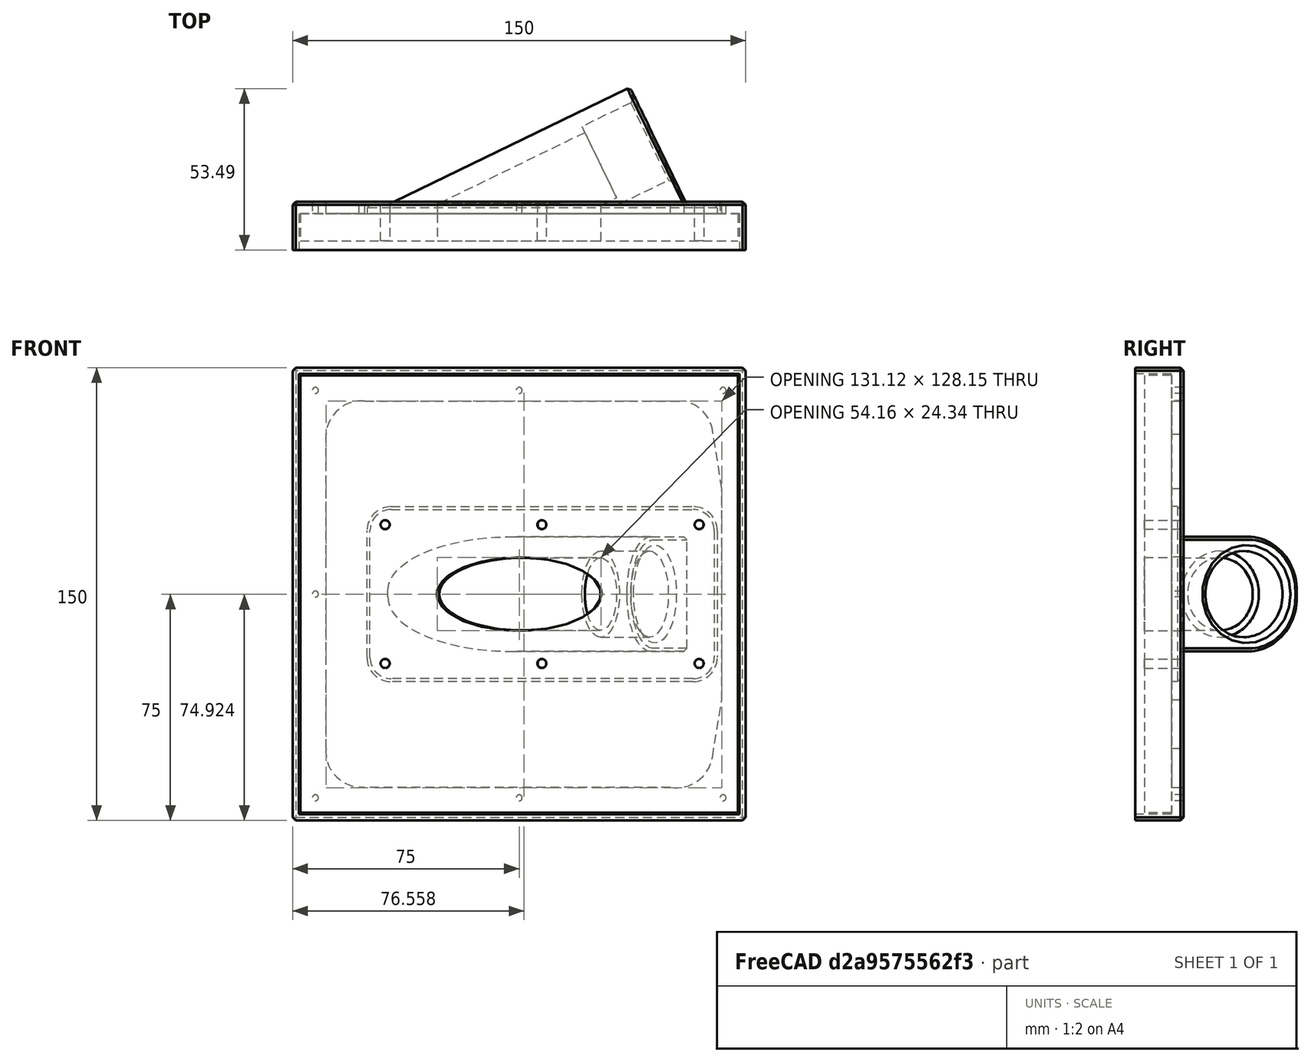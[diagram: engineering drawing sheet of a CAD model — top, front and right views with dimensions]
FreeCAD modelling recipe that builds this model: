
FCSTD DOCUMENT  (FreeCAD 0.19R)
Label: support_panneau_solaire_haut
License: All rights reserved
LicenseURL: http://en.wikipedia.org/wiki/All_rights_reserved
objects: Sketcher::SketchObject×8, PartDesign::Pad×5, PartDesign::Chamfer×4, PartDesign::Pocket×3, PartDesign::Body×3, PartDesign::Fillet×2, Mesh::Feature×2
note: 39 computed .brp shape members not serialized (recipe doc carries the construction recipe); baked Part::Feature solids carry a one-line shape summary decoded from their .brp

FEATURE [Sketcher::SketchObject] Sketch
  FullyConstrained = false
  MapMode = 5
  Support = -> [XY_Plane]
  sketch-geometry (3):
    g0: LineSegment StartX=19 StartY=-50 StartZ=0 EndX=19 EndY=39.129 EndZ=0
    g1: LineSegment StartX=19 StartY=39.129 StartZ=0 EndX=-24.2787 EndY=-50 EndZ=0
    g2: LineSegment StartX=-24.2787 StartY=-50 StartZ=0 EndX=19 EndY=-50 EndZ=0
  constraints (9):
    c: Horizontal(g2)
    c: Coincident(g0,g1)
    c: DistanceX(g-2,g0) = 19
    c: Vertical(g0)
    c: Angle(g1,g0) = 0.45204
    c: Coincident(g1,g2)
    c: Coincident(g2,g0)
    c: PointOnObject(g-1,g1)
    c: Distance(g-1,g2) = 50
FEATURE [PartDesign::Pad] Pad
  AllowMultiFace = false
  Direction = (1,1,1)
  Length = 38
  Length2 = 100
  Midplane = true
  Profile = -> Sketch
  Type = 0
FEATURE [Sketcher::SketchObject] Sketch001
  FullyConstrained = false
  MapMode = 5
  Placement = pos=(0,-50,0) rot=(1,0,0;1.5708rad)
  Support = -> [Pad]
  sketch-geometry (1):
    g0: Circle CenterX=0 CenterY=0 CenterZ=0 NormalX=0 NormalY=0 NormalZ=1 AngleXU=0 Radius=12
  constraints (2):
    c: Coincident(g0,g-1)
    c: Radius(g0) = 12
FEATURE [PartDesign::Pocket] Pocket
  AllowMultiFace = false
  BaseFeature = -> Pad
  Length = 100
  Length2 = 100
  Profile = -> Sketch001
  Type = 0
FEATURE [PartDesign::Fillet] Fillet
  Base = -> Pocket [Edge4,Edge3]
  BaseFeature = -> Pocket
  Radius = 18
  SupportTransform = false
FEATURE [Sketcher::SketchObject] Sketch002
  ExternalGeometry = -> [Fillet]
  FullyConstrained = false
  MapMode = 5
  Placement = pos=(0,-50,0) rot=(1,0,0;1.5708rad)
  Support = -> [Fillet]
  sketch-geometry (1):
    g0: Circle CenterX=0 CenterY=0 CenterZ=0 NormalX=0 NormalY=0 NormalZ=1 AngleXU=0 Radius=14.25
  constraints (2):
    c: Coincident(g0,g-1)
    c: Radius(g0) = 14.25
FEATURE [PartDesign::Pocket] Pocket001
  AllowMultiFace = false
  BaseFeature = -> Fillet
  Length = 20
  Length2 = 100
  Profile = -> Sketch002
  Type = 0
FEATURE [Sketcher::SketchObject] Sketch003
  ExternalGeometry = -> [Pocket001]
  FullyConstrained = true
  MapMode = 5
  Placement = pos=(-3.2e-15,1.6e-15,0) rot=(-0.404812,0.646578,0.646578;3.91089rad)
  Support = -> [Pocket001]
  sketch-geometry (14):
    g0: LineSegment StartX=-50.4171 StartY=29 StartZ=0 EndX=65.5829 EndY=29 EndZ=0
    g1: LineSegment StartX=65.5829 StartY=29 StartZ=0 EndX=65.5829 EndY=-29 EndZ=0
    g2: LineSegment StartX=65.5829 StartY=-29 StartZ=0 EndX=-50.4171 EndY=-29 EndZ=0
    g3: LineSegment StartX=-50.4171 StartY=-29 StartZ=0 EndX=-50.4171 EndY=29 EndZ=0
    g4: Circle CenterX=-44.4171 CenterY=23 CenterZ=0 NormalX=0 NormalY=0 NormalZ=1 AngleXU=0 Radius=1.5
    g5: Circle CenterX=-44.4171 CenterY=-23 CenterZ=0 NormalX=0 NormalY=0 NormalZ=1 AngleXU=0 Radius=1.5
    g6: Circle CenterX=59.5829 CenterY=23 CenterZ=0 NormalX=0 NormalY=0 NormalZ=1 AngleXU=0 Radius=1.5
    g7: Circle CenterX=59.5829 CenterY=-23 CenterZ=0 NormalX=0 NormalY=0 NormalZ=1 AngleXU=0 Radius=1.5
    g8: Circle CenterX=7.58287 CenterY=-23 CenterZ=0 NormalX=0 NormalY=0 NormalZ=1 AngleXU=0 Radius=1.5
    g9: Circle CenterX=7.58287 CenterY=23 CenterZ=0 NormalX=0 NormalY=0 NormalZ=1 AngleXU=0 Radius=1.5
    g10: LineSegment StartX=-44.4171 StartY=23 StartZ=0 EndX=59.5829 EndY=23 EndZ=0
    g11: LineSegment StartX=59.5829 StartY=23 StartZ=0 EndX=59.5829 EndY=-23 EndZ=0
    g12: LineSegment StartX=59.5829 StartY=-23 StartZ=0 EndX=-44.4171 EndY=-23 EndZ=0
    g13: LineSegment StartX=-44.4171 StartY=-23 StartZ=0 EndX=-44.4171 EndY=23 EndZ=0
  constraints (35):
    c: Coincident(g0,g1)
    c: Coincident(g1,g2)
    c: Coincident(g2,g3)
    c: Coincident(g3,g0)
    c: Horizontal(g2)
    c: Vertical(g1)
    c: Symmetric(g0,g2,g-1)
    c: Distance(g0,g-4) = 10
    c: Distance(g-4,g0) = 10
    c: Horizontal(g0)
    c: Coincident(g10,g11)
    c: Coincident(g11,g12)
    c: Coincident(g12,g13)
    c: Coincident(g13,g10)
    c: Horizontal(g10)
    c: Horizontal(g12)
    c: Vertical(g11)
    c: Coincident(g10,g4)
    c: Coincident(g11,g7)
    c: Coincident(g6,g10)
    c: PointOnObject(g9,g10)
    c: Coincident(g5,g12)
    c: Symmetric(g5,g4,g-1)
    c: Symmetric(g9,g8,g-1)
    c: Distance(g4,g0) = 6
    c: Distance(g4,g3) = 6
    c: Distance(g6,g1) = 6
    c: Radius(g4) = 1.5
    c: Equal(g4,g9)
    c: Equal(g4,g6)
    c: Equal(g4,g7)
    c: Equal(g4,g8)
    c: Equal(g4,g5)
    c: DistanceX(g12,g12) = 104
    c: Distance(g4,g9) = 52
FEATURE [PartDesign::Pad] Pad001
  AllowMultiFace = false
  BaseFeature = -> Pocket001
  Direction = (1,1,1)
  Length = 3
  Length2 = 100
  Profile = -> Sketch003
  Type = 0
FEATURE [Sketcher::SketchObject] Sketch009
  FullyConstrained = true
  MapMode = 5
  Placement = pos=(0,0,0) rot=(1,0,0;1.5708rad)
  Support = -> [XZ_Plane001]
  sketch-geometry (8):
    g0: LineSegment StartX=-73 StartY=73 StartZ=0 EndX=73 EndY=73 EndZ=0
    g1: LineSegment StartX=73 StartY=73 StartZ=0 EndX=73 EndY=-73 EndZ=0
    g2: LineSegment StartX=73 StartY=-73 StartZ=0 EndX=-73 EndY=-73 EndZ=0
    g3: LineSegment StartX=-73 StartY=-73 StartZ=0 EndX=-73 EndY=73 EndZ=0
    g4: LineSegment StartX=-75 StartY=75 StartZ=0 EndX=75 EndY=75 EndZ=0
    g5: LineSegment StartX=75 StartY=75 StartZ=0 EndX=75 EndY=-75 EndZ=0
    g6: LineSegment StartX=75 StartY=-75 StartZ=0 EndX=-75 EndY=-75 EndZ=0
    g7: LineSegment StartX=-75 StartY=-75 StartZ=0 EndX=-75 EndY=75 EndZ=0
  constraints (20):
    c: Coincident(g0,g1)
    c: Coincident(g1,g2)
    c: Coincident(g2,g3)
    c: Coincident(g3,g0)
    c: Horizontal(g2)
    c: Vertical(g1)
    c: Symmetric(g0,g2,g-1)
    c: Symmetric(g0,g0,g-2)
    c: Equal(g0,g3)
    c: DistanceY(g3,g3) = 146
    c: Coincident(g4,g5)
    c: Coincident(g5,g6)
    c: Coincident(g6,g7)
    c: Coincident(g7,g4)
    c: Horizontal(g6)
    c: Vertical(g7)
    c: Distance(g4,g3) = 2
    c: Distance(g4,g0) = 2
    c: Symmetric(g4,g4,g-2)
    c: Symmetric(g4,g5,g-1)
FEATURE [PartDesign::Pad] Pad003
  AllowMultiFace = false
  Direction = (1,1,1)
  Length = 12
  Length2 = 100
  Placement = pos=(0,0,0) rot=(1,0,0;1.5708rad)
  Profile = -> Sketch009
  Type = 0
FEATURE [Sketcher::SketchObject] Sketch010
  ExternalGeometry = -> [Pad003]
  FullyConstrained = true
  MapMode = 5
  Placement = pos=(0,0,0) rot=(-1,0,0;1.5708rad)
  Support = -> [Pad003]
  sketch-geometry (21):
    g0: LineSegment StartX=-75 StartY=75 StartZ=0 EndX=75 EndY=75 EndZ=0
    g1: LineSegment StartX=75 StartY=75 StartZ=0 EndX=75 EndY=-75 EndZ=0
    g2: LineSegment StartX=75 StartY=-75 StartZ=0 EndX=-75 EndY=-75 EndZ=0
    g3: LineSegment StartX=-75 StartY=-75 StartZ=0 EndX=-75 EndY=75 EndZ=0
    g4: ArcOfCircle CenterX=-52.0386 CenterY=52.0386 CenterZ=0 NormalX=0 NormalY=0 NormalZ=1 AngleXU=0 Radius=12 StartAngle=1.651 EndAngle=3.2218
    g5: ArcOfCircle CenterX=52.0386 CenterY=52.0386 CenterZ=0 NormalX=0 NormalY=0 NormalZ=1 AngleXU=0 Radius=12.1212 StartAngle=0.162533 EndAngle=1.73333
    g6: ArcOfCircle CenterX=52.0386 CenterY=-52.0386 CenterZ=0 NormalX=0 NormalY=0 NormalZ=1 AngleXU=0 Radius=12.2353 StartAngle=4.92436 EndAngle=6.12218
    g7: ArcOfCircle CenterX=-52.0386 CenterY=-52.0386 CenterZ=0 NormalX=0 NormalY=0 NormalZ=1 AngleXU=0 Radius=12 StartAngle=3.2218 EndAngle=4.79259
    g8: LineSegment StartX=-64 StartY=51.0772 StartZ=0 EndX=-64 EndY=-53 EndZ=0
    g9: LineSegment StartX=-51.0772 StartY=-64 StartZ=0 EndX=54.6127 EndY=-64 EndZ=0
    g10: LineSegment StartX=50.0772 StartY=64 StartZ=0 EndX=-53 EndY=64 EndZ=0
    g11: Circle CenterX=-67.5 CenterY=67.5 CenterZ=0 NormalX=0 NormalY=0 NormalZ=1 AngleXU=0 Radius=1
    g12: Circle CenterX=67.5 CenterY=67.5 CenterZ=0 NormalX=0 NormalY=0 NormalZ=1 AngleXU=0 Radius=1
    g13: Circle CenterX=0 CenterY=67.5 CenterZ=0 NormalX=0 NormalY=0 NormalZ=1 AngleXU=0 Radius=1
    g14: Circle CenterX=-67.5 CenterY=0 CenterZ=0 NormalX=0 NormalY=0 NormalZ=1 AngleXU=0 Radius=1
    g15: Circle CenterX=-67.5 CenterY=-67.5 CenterZ=0 NormalX=0 NormalY=0 NormalZ=1 AngleXU=0 Radius=1
    g16: Circle CenterX=0 CenterY=-67.5 CenterZ=0 NormalX=0 NormalY=0 NormalZ=1 AngleXU=0 Radius=1
    g17: Circle CenterX=67.5 CenterY=-67.5 CenterZ=0 NormalX=0 NormalY=0 NormalZ=1 AngleXU=0 Radius=1
    g18: LineSegment StartX=64 StartY=54 StartZ=0 EndX=67.1156 EndY=35 EndZ=0
    g19: LineSegment StartX=67.1156 StartY=35 StartZ=0 EndX=67.1156 EndY=-35 EndZ=0
    g20: LineSegment StartX=67.1156 StartY=-35 StartZ=0 EndX=64.1156 EndY=-54 EndZ=0
  constraints (54):
    c: Coincident(g0,g1)
    c: Coincident(g1,g2)
    c: Coincident(g2,g3)
    c: Coincident(g3,g0)
    c: Horizontal(g0)
    c: Horizontal(g2)
    c: Vertical(g1)
    c: Vertical(g3)
    c: Coincident(g0,g-4)
    c: Coincident(g1,g-6)
    c: Coincident(g8,g4)
    c: Coincident(g8,g7)
    c: Vertical(g8)
    c: Coincident(g9,g7)
    c: Coincident(g9,g6)
    c: Horizontal(g9)
    c: Coincident(g10,g5)
    c: Coincident(g10,g4)
    c: Radius(g4) = 12
    c: Angle(g7) = 1.5708
    c: Angle(g4) = 1.5708
    c: Angle(g5) = 1.5708
    c: Symmetric(g7,g6,g-2)
    c: Symmetric(g7,g4,g-1)
    c: Symmetric(g5,g6,g-1)
    c: Distance(g4,g3) = 11
    c: Distance(g4,g0) = 11
    c: Horizontal(g10)
    c: Distance(g5,g0) = 21
    c: Distance(g6,g2) = 21
    c: PointOnObject(g16,g-2)
    c: Distance(g17,g1) = 7.5
    c: Distance(g17,g2) = 7.5
    c: Distance(g16,g2) = 7.5
    c: Distance(g15,g2) = 7.5
    c: Distance(g15,g3) = 7.5
    c: PointOnObject(g14,g-1)
    c: Distance(g14,g3) = 7.5
    c: Symmetric(g15,g11,g-1)
    c: Symmetric(g16,g13,g-1)
    c: Symmetric(g12,g17,g-1)
    c: Distance(g4,g3) = 22
    c: Distance(g7,g2) = 22
    c: Tangent(g5,g18) = 1.5708
    c: Coincident(g18,g19)
    c: Coincident(g19,g20)
    c: Coincident(g20,g6)
    c: Symmetric(g19,g18,g-1)
    c: Radius(g12) = 1
    c: Equal(g12,g13)
    c: Equal(g12,g11)
    c: Equal(g12, g14-g17) x4
    c: DistanceY(g19,g19) = 70
    c: Distance(g6,g19) = 3
FEATURE [PartDesign::Pad] Pad004
  AllowMultiFace = false
  BaseFeature = -> Pad003
  Direction = (1,1,1)
  Length = 4
  Length2 = 100
  Placement = pos=(0,0,0) rot=(1,0,0;1.5708rad)
  Profile = -> Sketch010
  Type = 0
FEATURE [PartDesign::Chamfer] Chamfer003
  Angle = 45
  Base = -> Pad004 [Edge24,Edge21,Edge13,Edge23,Edge22,Edge2,Edge5,Edge1]
  BaseFeature = -> Pad004
  ChamferType = 0
  FlipDirection = false
  Placement = pos=(0,0,0) rot=(1,0,0;1.5708rad)
  Size = 1
  Size2 = 1
  SupportTransform = false
FEATURE [PartDesign::Body] Body001  label="Contour"
  Group = -> [Sketch009,Pad003,Sketch010,Pad004,Chamfer003]
  Origin = -> Origin001
  Placement = pos=(0,-3,0) rot=(0,0,1;0rad)
  Tip = -> Chamfer003
FEATURE [Mesh::Feature] Mesh001  label="Contour (Meshed)"
FEATURE [Sketcher::SketchObject] Sketch011
  FullyConstrained = true
  MapMode = 5
  Placement = pos=(-2.69867,1.31041,0) rot=(-0.404812,0.646578,0.646578;3.91089rad)
  Support = -> [Pad001]
  sketch-geometry (5):
    g0: Ellipse CenterX=0 CenterY=0 CenterZ=0 NormalX=0 NormalY=0 NormalZ=1 MajorRadius=27 MinorRadius=12.25 AngleXU=-3.14159
    g1: LineSegment StartX=-27 StartY=0 StartZ=0 EndX=27 EndY=0 EndZ=0
    g2: LineSegment StartX=0 StartY=-12.25 StartZ=0 EndX=0 EndY=12.25 EndZ=0
    g3: GeomPoint X=-24.0611 Y=0 Z=0
    g4: GeomPoint X=24.0611 Y=0 Z=0
  constraints (5):
    c: InternalAlignment(g1-g4 -> g0) x4
    c: Distance(g1,g0) = 27
    c: Distance(g2,g0) = 12.25
    c: Coincident(g0,g-1)
    c: PointOnObject(g3,g-1)
FEATURE [PartDesign::Pocket] Pocket002
  BaseFeature = -> Pad001
  Length = 3.5
  Length2 = 100
  Profile = -> Sketch011
  Type = 0
FEATURE [PartDesign::Fillet] Fillet001
  Base = -> Pocket002 [Edge2,Edge8,Edge5,Edge1]
  BaseFeature = -> Pocket002
  Radius = 8
  SupportTransform = false
FEATURE [PartDesign::Chamfer] Chamfer
  Angle = 45
  Base = -> Fillet001 [Edge55]
  BaseFeature = -> Fillet001
  ChamferType = 0
  FlipDirection = false
  Size = 2
  Size2 = 1
  SupportTransform = false
FEATURE [PartDesign::Chamfer] Chamfer004
  Angle = 45
  Base = -> Chamfer [Edge2]
  BaseFeature = -> Chamfer
  ChamferType = 0
  FlipDirection = false
  Size = 1
  Size2 = 1
  SupportTransform = false
FEATURE [PartDesign::Chamfer] Chamfer005
  Angle = 45
  Base = -> Chamfer004 [Edge22]
  BaseFeature = -> Chamfer004
  ChamferType = 0
  FlipDirection = false
  Size = 1
  Size2 = 1
  SupportTransform = false
FEATURE [PartDesign::Body] Body  label="fixation_mat"
  Group = -> [Sketch,Pad,Sketch001,Pocket,Fillet,Sketch002,Pocket001,Sketch003,Pad001,Sketch011,Pocket002,Fillet001,Chamfer,Chamfer004,Chamfer005]
  Origin = -> Origin
  Placement = pos=(0,0,0) rot=(0,0,1;2.02284rad)
  Tip = -> Chamfer005
FEATURE [Mesh::Feature] Mesh  label="Body (Meshed)"
FEATURE [Sketcher::SketchObject] Sketch012
  FullyConstrained = true
  MapMode = 5
  Placement = pos=(0,0,0) rot=(1,0,0;1.5708rad)
  Support = -> [XZ_Plane002]
  sketch-geometry (15):
    g0: LineSegment StartX=-72.5 StartY=72.5 StartZ=0 EndX=72.5 EndY=72.5 EndZ=0
    g1: LineSegment StartX=72.5 StartY=72.5 StartZ=0 EndX=72.5 EndY=-72.5 EndZ=0
    g2: LineSegment StartX=72.5 StartY=-72.5 StartZ=0 EndX=-72.5 EndY=-72.5 EndZ=0
    g3: LineSegment StartX=-72.5 StartY=-72.5 StartZ=0 EndX=-72.5 EndY=72.5 EndZ=0
    g4: Circle CenterX=-44.4 CenterY=23 CenterZ=0 NormalX=0 NormalY=0 NormalZ=1 AngleXU=0 Radius=1.5
    g5: Circle CenterX=-44.4 CenterY=-23 CenterZ=0 NormalX=0 NormalY=0 NormalZ=1 AngleXU=0 Radius=1.5
    g6: Circle CenterX=7.5 CenterY=-23 CenterZ=0 NormalX=0 NormalY=0 NormalZ=1 AngleXU=0 Radius=1.5
    g7: Circle CenterX=7.5 CenterY=23 CenterZ=0 NormalX=0 NormalY=0 NormalZ=1 AngleXU=0 Radius=1.5
    g8: Circle CenterX=59.6 CenterY=23 CenterZ=0 NormalX=0 NormalY=0 NormalZ=1 AngleXU=0 Radius=1.5
    g9: Circle CenterX=59.6 CenterY=-23 CenterZ=0 NormalX=0 NormalY=0 NormalZ=1 AngleXU=0 Radius=1.5
    g10: Ellipse CenterX=0 CenterY=0 CenterZ=0 NormalX=0 NormalY=0 NormalZ=1 MajorRadius=27.08 MinorRadius=12.17 AngleXU=-3.14159
    g11: LineSegment StartX=-27.08 StartY=0 StartZ=0 EndX=27.08 EndY=0 EndZ=0
    g12: LineSegment StartX=0 StartY=-12.17 StartZ=0 EndX=0 EndY=12.17 EndZ=0
    g13: GeomPoint X=-24.1913 Y=0 Z=0
    g14: GeomPoint X=24.1913 Y=0 Z=0
  constraints (31):
    c: Coincident(g0,g1)
    c: Coincident(g1,g2)
    c: Coincident(g2,g3)
    c: Coincident(g3,g0)
    c: Horizontal(g0)
    c: Horizontal(g2)
    c: Vertical(g1)
    c: Vertical(g3)
    c: Symmetric(g1,g0,g-1)
    c: Equal(g3,g0)
    c: DistanceX(g0,g0) = 145
    c: Symmetric(g9,g8,g-1)
    c: Symmetric(g7,g6,g-1)
    c: Symmetric(g4,g5,g-1)
    c: DistanceX(g-2,g4) = -44.4
    c: DistanceX(g-2,g7) = 7.5
    c: DistanceX(g-2,g8) = 59.6
    c: DistanceY(g-1,g7) = 23
    c: DistanceY(g-1,g8) = 23
    c: DistanceY(g-1,g4) = 23
    c: Radius(g5) = 1.5
    c: Equal(g5,g6)
    c: Equal(g5,g9)
    c: Equal(g5,g8)
    c: Equal(g5,g7)
    c: Equal(g5,g4)
    c: InternalAlignment(g11-g14 -> g10) x4
    c: Coincident(g10,g-1)
    c: PointOnObject(g11,g-1)
    c: Distance(g11,g12) = 27.08
    c: DistanceY(g-1,g12) = 12.17
FEATURE [PartDesign::Pad] Pad005
  Direction = (1,1,1)
  Length = 9
  Length2 = 100
  Placement = pos=(0,0,0) rot=(1,0,0;1.5708rad)
  Profile = -> Sketch012
  Type = 0
FEATURE [PartDesign::Body] Body002  label="base_carree"
  Group = -> [Sketch012,Pad005]
  Origin = -> Origin002
  Placement = pos=(0,-3,0) rot=(0,0,1;0rad)
  Tip = -> Pad005
